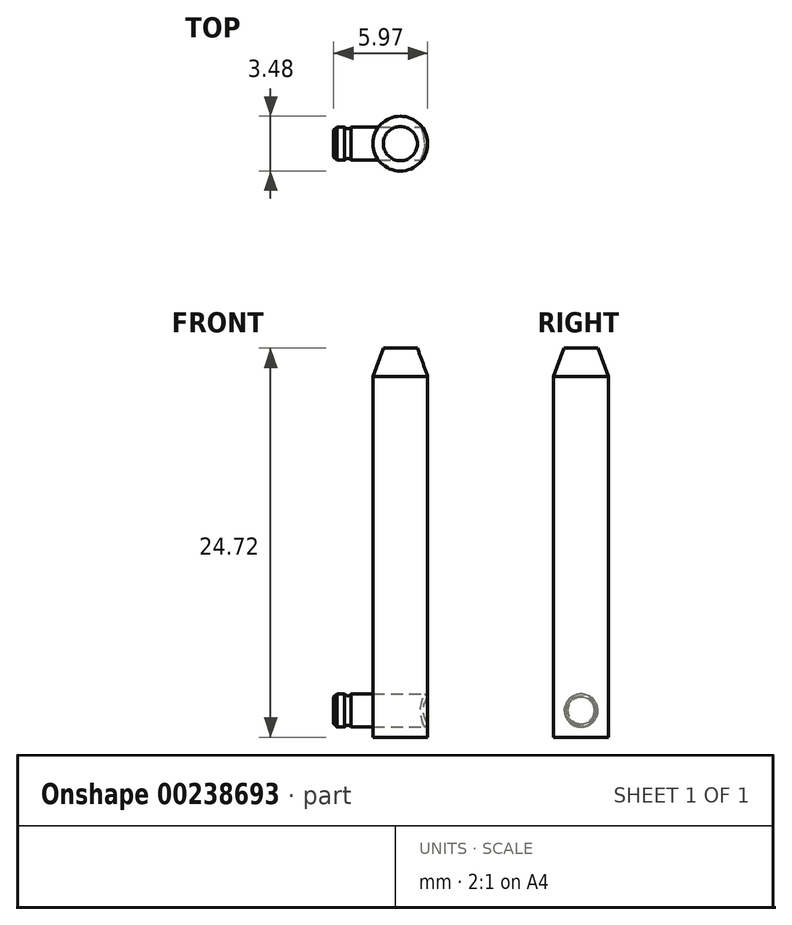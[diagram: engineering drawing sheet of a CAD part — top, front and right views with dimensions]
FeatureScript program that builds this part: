
annotation { "Feature Type Name" : "Feature", "Feature Type Description" : "" }
export const myFeature = defineFeature(function(context is Context, id is Id, definition is map)
    precondition{}
    {
        {
            var Q0;
            Q0=qCreatedBy(makeId("Top.planeOp"),FACE);
            var sketch = newSketch(context, id + "F0", { "sketchPlane" : qUnion([Q0])});
            skCircle(sketch, "E0", {"center": v(0, 0) * mm, "radius": 1.74 * mm});
            skSolve(sketch);
        }
        {
            var Q0;
            Q0=makeQuery(id+"F0.imprint","IMPRINT",FACE,{"disambiguationData":[TD([[makeQuery(id+"F0.imprint","IMPRINT",EDGE,{"derivedFrom":sQuery(id+"F0.wireOp",EDGE,"E0")}),1.0]])]});
            extrude(context, id + "F1", {"entities" : qUnion([Q0]), "depth" : 24.72 * mm});
        }
        {
            var Q0;
            Q0=makeQuery(id+"F1.opExtrude","CAP_EDGE",EDGE,{"disambiguationData":[OSD([sQuery(id+"F0.wireOp",EDGE,"E0")])],"isStart":false});
            chamfer(context, id + "F2", {"entities" : qUnion([Q0]), "chamferType" : ChamferType.OFFSET_ANGLE, "width" : 1.8 * mm, "oppositeDirection" : true, "angle" : 20 * degree});
        }
        {
            var Q0;
            Q0=qCreatedBy(makeId("Right.planeOp"),FACE);
            var sketch = newSketch(context, id + "F3", { "sketchPlane" : qUnion([Q0])});
            skCircle(sketch, "E1", {"center": v(0, 1.7) * mm, "radius": 1.05 * mm});
            skSolve(sketch);
        }
        {
            var Q0;
            Q0=makeQuery(id+"F3.imprint","IMPRINT",FACE,{"disambiguationData":[TD([[makeQuery(id+"F3.imprint","IMPRINT",EDGE,{"derivedFrom":sQuery(id+"F3.wireOp",EDGE,"E1")}),1.0]])]});
            extrude(context, id + "F4", {"entities" : qUnion([Q0]), "oppositeDirection" : true, "depth" : 4.23 * mm, "hasSecondDirection" : true, "secondDirectionBound" : SecondDirectionBoundingType.UP_TO_NEXT, "secondDirectionOppositeDirection" : false, "secondDirectionDepth" : 25 * mm});
        }
        {
            var Q0;
            Q0=qCreatedBy(makeId("Front.planeOp"),FACE);
            var sketch = newSketch(context, id + "F5", { "sketchPlane" : qUnion([Q0])});
            skLineSegment(sketch, "E2", {"start": v(-3.58, 4.6) * mm, "end": v(-3.58, 2.9) * mm});
            skLineSegment(sketch, "E3", {"start": v(-3.08, 4.6) * mm, "end": v(-3.08, 2.9) * mm});
            skLineSegment(sketch, "E4", {"start": v(-3.58, 4.6) * mm, "end": v(-3.08, 4.6) * mm});
            skArc(sketch, "E5", {"start": v(-3.58, 2.9) * mm, "mid": v(-3.33, 2.64) * mm, "end": v(-3.08, 2.9) * mm});
            skSolve(sketch);
        }
        {
            var Q0;
            Q0=makeQuery(id+"F5.imprint","IMPRINT",FACE,{"disambiguationData":[TD([[makeQuery(id+"F5.imprint","IMPRINT",EDGE,{"derivedFrom":sQuery(id+"F5.wireOp",EDGE,"E2")}),1.0]])]});
            var Q1;
            Q1=makeQuery(id+"F4.opExtrude","SWEPT_FACE",FACE,{"disambiguationData":[OSD([sQuery(id+"F3.wireOp",EDGE,"E1")])]});
            revolve(context, id + "F6", {"operationType" : NewBodyOperationType.REMOVE, "entities" : qUnion([Q0]), "axis" : qUnion([Q1]), "revolveType" : RevolveType.FULL, "oppositeDirection" : true});
        }
        {
            var Q0;
            Q0=makeQuery(id+"F4.opExtrude","CAP_EDGE",EDGE,{"disambiguationData":[OSD([sQuery(id+"F3.wireOp",EDGE,"E1")])],"isStart":false});
            chamfer(context, id + "F7", {"entities" : qUnion([Q0]), "width" : 0.2 * mm, "tangentPropagation" : true});
        }
    });
